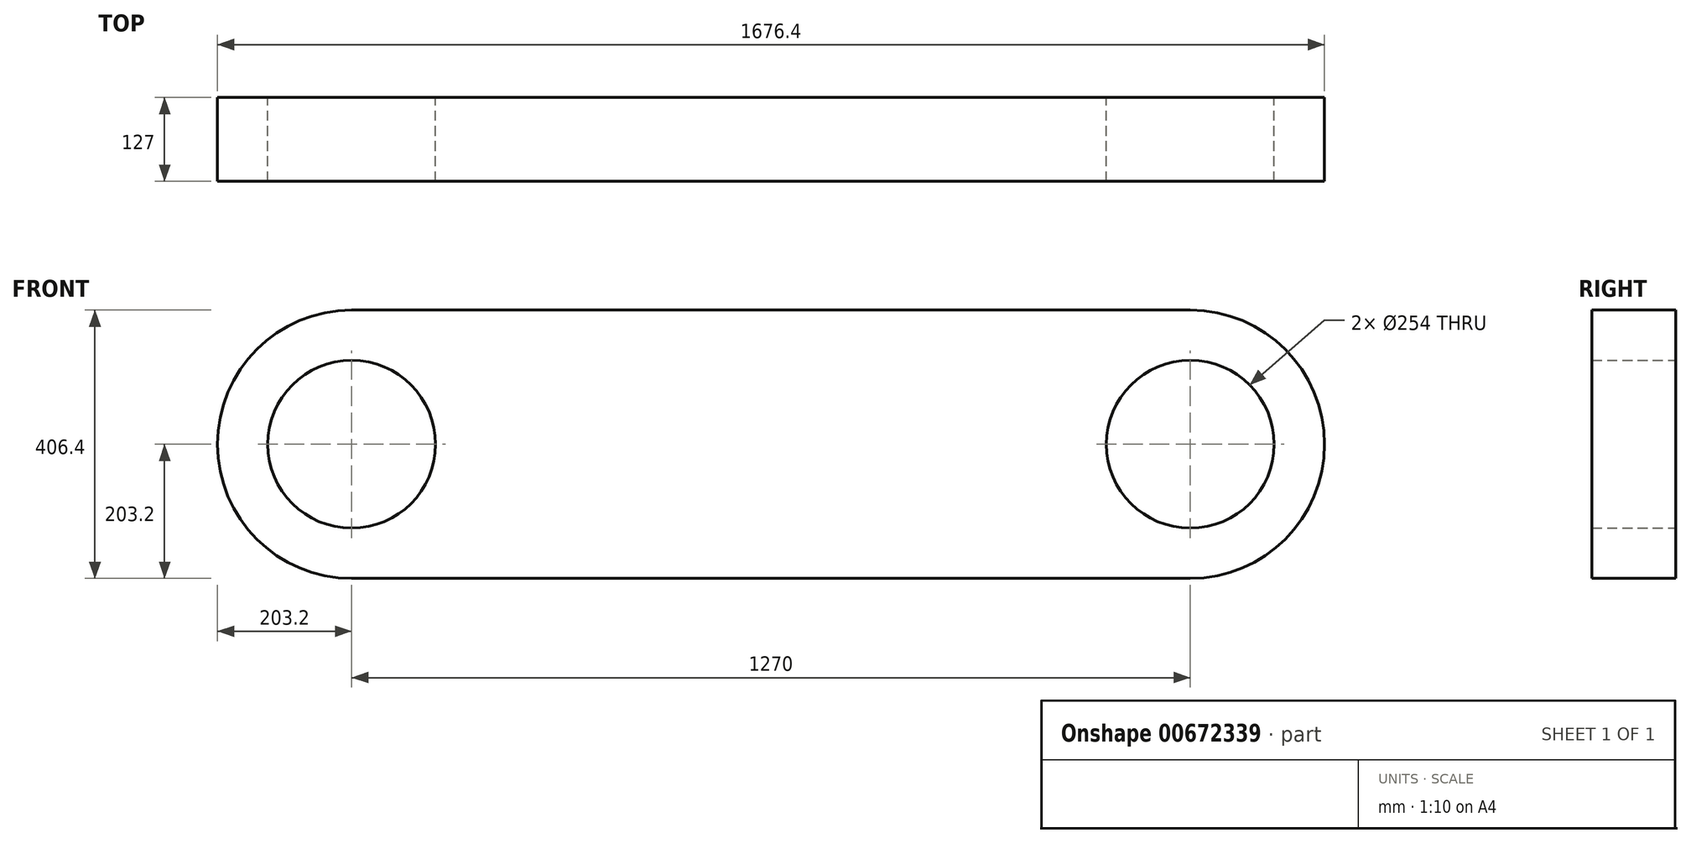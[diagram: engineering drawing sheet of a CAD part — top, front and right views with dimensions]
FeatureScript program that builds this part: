
annotation { "Feature Type Name" : "Feature", "Feature Type Description" : "" }
export const myFeature = defineFeature(function(context is Context, id is Id, definition is map)
    precondition{}
    {
        {
            var Q0;
            Q0=qCreatedBy(makeId("Front.planeOp"),FACE);
            var sketch = newSketch(context, id + "F0", { "sketchPlane" : qUnion([Q0])});
            skLineSegment(sketch, "E0.bottom", {"start": v(-635, 203.2) * mm, "end": v(635, 203.2) * mm});
            skLineSegment(sketch, "E0.top", {"start": v(-635, -203.2) * mm, "end": v(635, -203.2) * mm});
            skArc(sketch, "E1", {"start": v(-635, 203.2) * mm, "mid": v(-838.2, 0) * mm, "end": v(-635, -203.2) * mm});
            skArc(sketch, "E2", {"start": v(635, -203.2) * mm, "mid": v(838.2, 0) * mm, "end": v(635, 203.2) * mm});
            skCircle(sketch, "E3", {"center": v(-635, 0) * mm, "radius": 127 * mm});
            skCircle(sketch, "E4", {"center": v(635, 0) * mm, "radius": 127 * mm});
            skSolve(sketch);
        }
        {
            var Q0;
            Q0 = qSketchRegion(id + "F0", true);
            extrude(context, id + "F1", {"entities" : qUnion([Q0]), "depth" : 127 * mm, "offsetDistance" : 25.4 * mm});
        }
    });
